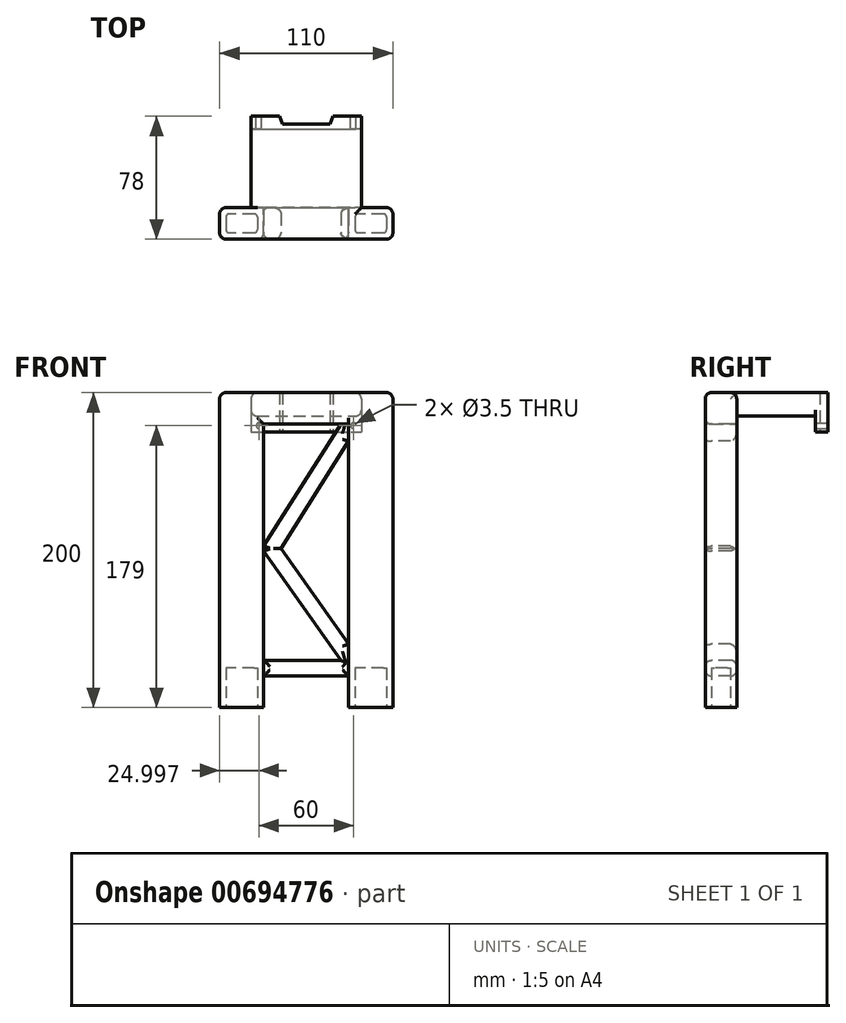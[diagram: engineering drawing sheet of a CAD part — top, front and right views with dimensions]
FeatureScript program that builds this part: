
annotation { "Feature Type Name" : "Feature", "Feature Type Description" : "" }
export const myFeature = defineFeature(function(context is Context, id is Id, definition is map)
    precondition{}
    {
        {
            var Q0;
            Q0=qCreatedBy(makeId("Top.planeOp"),FACE);
            var sketch = newSketch(context, id + "F0", { "sketchPlane" : qUnion([Q0])});
            skLineSegment(sketch, "E0.bottom", {"start": v(-48.83, 24.85) * mm, "end": v(-30.83, 24.85) * mm});
            skLineSegment(sketch, "E0.top", {"start": v(-48.83, 16.85) * mm, "end": v(21.17, 16.85) * mm});
            skLineSegment(sketch, "E0.left", {"start": v(-48.83, 24.85) * mm, "end": v(-48.83, 16.85) * mm});
            skLineSegment(sketch, "E0.right", {"start": v(21.17, 24.85) * mm, "end": v(21.17, 16.85) * mm});
            skLineSegment(sketch, "E1", {"start": v(-30.83, 24.85) * mm, "end": v(-28.83, 19.85) * mm});
            skLineSegment(sketch, "E2", {"start": v(-28.83, 19.85) * mm, "end": v(1.17, 19.85) * mm});
            skLineSegment(sketch, "E3", {"start": v(1.17, 19.85) * mm, "end": v(3.17, 24.85) * mm});
            skLineSegment(sketch, "E4.trimOffspring", {"start": v(3.17, 24.85) * mm, "end": v(21.17, 24.85) * mm});
            skSolve(sketch);
        }
        {
            var Q0;
            Q0=makeQuery(id+"F0.imprint","IMPRINT",FACE,{"disambiguationData":[TD([[makeQuery(id+"F0.imprint","IMPRINT",EDGE,{"derivedFrom":sQuery(id+"F0.wireOp",EDGE,"E0.bottom")}),-1.0]])]});
            extrude(context, id + "F1", {"entities" : qUnion([Q0]), "depth" : 25 * mm, "offsetDistance" : 25 * mm});
        }
        {
            var Q0;
            Q0=makeQuery(id+"F1.opExtrude","SWEPT_FACE",FACE,{"disambiguationData":[OSD([sQuery(id+"F0.wireOp",EDGE,"E0.bottom")])]});
            var sketch = newSketch(context, id + "F2", { "sketchPlane" : qUnion([Q0])});
            skCircle(sketch, "E5", {"center": v(-16.17, 4) * mm, "radius": 1.75 * mm});
            skCircle(sketch, "E6", {"center": v(43.83, 4) * mm, "radius": 1.75 * mm});
            skSolve(sketch);
        }
        {
            var Q0;
            Q0=makeQuery(id+"F2.imprint","IMPRINT",FACE,{"disambiguationData":[TD([[makeQuery(id+"F2.imprint","IMPRINT",EDGE,{"derivedFrom":sQuery(id+"F2.wireOp",EDGE,"E5")}),1.0]])]});
            var Q1;
            Q1=makeQuery(id+"F2.imprint","IMPRINT",FACE,{"disambiguationData":[TD([[makeQuery(id+"F2.imprint","IMPRINT",EDGE,{"derivedFrom":sQuery(id+"F2.wireOp",EDGE,"E6")}),1.0]])]});
            extrude(context, id + "F3", {"entities" : qUnion([Q0, Q1]), "operationType" : NewBodyOperationType.REMOVE, "oppositeDirection" : true, "depth" : 25 * mm, "offsetDistance" : 25 * mm});
        }
        {
            var Q0;
            Q0=makeQuery(id+"F1.opExtrude","SWEPT_FACE",FACE,{"disambiguationData":[OSD([sQuery(id+"F0.wireOp",EDGE,"E0.top")])]});
            var sketch = newSketch(context, id + "F4", { "sketchPlane" : qUnion([Q0])});
            skLineSegment(sketch, "E7.bottom", {"start": v(-48.83, 25) * mm, "end": v(21.17, 25) * mm});
            skLineSegment(sketch, "E7.top", {"start": v(-48.83, 10) * mm, "end": v(21.17, 10) * mm});
            skLineSegment(sketch, "E7.left", {"start": v(-48.83, 25) * mm, "end": v(-48.83, 10) * mm});
            skLineSegment(sketch, "E7.right", {"start": v(21.17, 25) * mm, "end": v(21.17, 10) * mm});
            skSolve(sketch);
        }
        {
            var Q0;
            Q0=makeQuery(id+"F4.imprint","IMPRINT",FACE,{"disambiguationData":[TD([[makeQuery(id+"F4.imprint","IMPRINT",EDGE,{"derivedFrom":sQuery(id+"F4.wireOp",EDGE,"E7.bottom")}),-1.0]])]});
            extrude(context, id + "F5", {"entities" : qUnion([Q0]), "operationType" : NewBodyOperationType.ADD, "depth" : 50 * mm, "offsetDistance" : 25 * mm});
        }
        {
            var Q0;
            Q0=makeQuery(id+"F5.boolean.opBoolean","MERGE",FACE,{"derivedFrom":[makeQuery(id+"F1.opExtrude","SWEPT_FACE",FACE,{"disambiguationData":[OSD([sQuery(id+"F0.wireOp",EDGE,"E0.right")])]}),makeQuery(id+"F5.opExtrude","SWEPT_FACE",FACE,{"disambiguationData":[OSD([sQuery(id+"F4.wireOp",EDGE,"E7.right")])]})]});
            var sketch = newSketch(context, id + "F6", { "sketchPlane" : qUnion([Q0])});
            skLineSegment(sketch, "E8.bottom", {"start": v(-33.15, 25) * mm, "end": v(-53.15, 25) * mm});
            skLineSegment(sketch, "E8.top", {"start": v(-33.15, -175) * mm, "end": v(-53.15, -175) * mm});
            skLineSegment(sketch, "E8.left", {"start": v(-33.15, 25) * mm, "end": v(-33.15, -175) * mm});
            skLineSegment(sketch, "E8.right", {"start": v(-53.15, 25) * mm, "end": v(-53.15, -175) * mm});
            skSolve(sketch);
        }
        {
            var Q0;
            {var subQ1=sQuery(id+"F6.wireOp",EDGE,"E8.bottom");Q0=makeQuery(id+"F6.imprint","IMPRINT",FACE,{"disambiguationData":[TD([[makeQuery(id+"F6.imprint","IMPRINT",EDGE,{"derivedFrom":subQ1}),1.0]])]});}
            extrude(context, id + "F7", {"entities" : qUnion([Q0]), "operationType" : NewBodyOperationType.ADD, "depth" : 20 * mm, "offsetDistance" : 25 * mm, "hasSecondDirection" : true, "secondDirectionOppositeDirection" : true, "secondDirectionDepth" : 90 * mm});
        }
        {
            var Q0;
            Q0=makeQuery(id+"F7.opExtrude","SWEPT_FACE",FACE,{"disambiguationData":[OSD([sQuery(id+"F6.wireOp",EDGE,"E8.left")])]});
            var sketch = newSketch(context, id + "F8", { "sketchPlane" : qUnion([Q0])});
            skLineSegment(sketch, "E9.bottom", {"start": v(-13.17, 5) * mm, "end": v(40.83, 5) * mm});
            skLineSegment(sketch, "E9.top", {"start": v(-13.17, -175) * mm, "end": v(40.83, -175) * mm});
            skLineSegment(sketch, "E9.left", {"start": v(-13.17, 5) * mm, "end": v(-13.17, -175) * mm});
            skLineSegment(sketch, "E9.right", {"start": v(40.83, 5) * mm, "end": v(40.83, -175) * mm});
            skSolve(sketch);
        }
        {
            var Q0;
            Q0=makeQuery(id+"F8.imprint","IMPRINT",FACE,{"disambiguationData":[TD([[makeQuery(id+"F8.imprint","IMPRINT",EDGE,{"derivedFrom":sQuery(id+"F8.wireOp",EDGE,"E9.bottom")}),-1.0]])]});
            extrude(context, id + "F9", {"entities" : qUnion([Q0]), "operationType" : NewBodyOperationType.REMOVE, "oppositeDirection" : true, "depth" : 25 * mm, "offsetDistance" : 25 * mm});
        }
        {
            var Q0;
            {var subQ2=sQuery(id+"F6.wireOp",EDGE,"E8.top");Q0=makeQuery(id+"F9.boolean.opBoolean","SPLIT",FACE,{"disambiguationData":[TD([makeQuery(id+"F9.opExtrude","SWEPT_FACE",FACE,{"disambiguationData":[OSD([sQuery(id+"F8.wireOp",EDGE,"E9.left")])]})])],"derivedFrom":makeQuery(id+"F7.opExtrude","SWEPT_FACE",FACE,{"disambiguationData":[OSD([subQ2])]})});}
            var sketch = newSketch(context, id + "F10", { "sketchPlane" : qUnion([Q0])});
            skLineSegment(sketch, "E10.bottom", {"start": v(35.17, 37.15) * mm, "end": v(19.17, 37.15) * mm});
            skLineSegment(sketch, "E10.top", {"start": v(35.17, 49.15) * mm, "end": v(19.17, 49.15) * mm});
            skLineSegment(sketch, "E10.left", {"start": v(37.17, 39.15) * mm, "end": v(37.17, 47.15) * mm});
            skLineSegment(sketch, "E10.right", {"start": v(17.17, 39.15) * mm, "end": v(17.17, 47.15) * mm});
            skLineSegment(sketch, "E11.bottom", {"start": v(-46.83, 37.15) * mm, "end": v(-62.83, 37.15) * mm});
            skLineSegment(sketch, "E11.top", {"start": v(-46.83, 49.15) * mm, "end": v(-62.83, 49.15) * mm});
            skLineSegment(sketch, "E11.left", {"start": v(-44.83, 39.15) * mm, "end": v(-44.83, 47.15) * mm});
            skLineSegment(sketch, "E11.right", {"start": v(-64.83, 39.15) * mm, "end": v(-64.83, 47.15) * mm});
            skPoint(sketch, "E12.visualSharp", {"position": v(-64.83, 37.15) * mm});
            skArc(sketch, "E12.filletArc", {"start": v(-64.83, 39.15) * mm, "mid": v(-64.25, 37.74) * mm, "end": v(-62.83, 37.15) * mm});
            skPoint(sketch, "E13.visualSharp", {"position": v(-64.83, 49.15) * mm});
            skArc(sketch, "E13.filletArc", {"start": v(-62.83, 49.15) * mm, "mid": v(-64.25, 48.56) * mm, "end": v(-64.83, 47.15) * mm});
            skPoint(sketch, "E14.visualSharp", {"position": v(-44.83, 49.15) * mm});
            skArc(sketch, "E14.filletArc", {"start": v(-44.83, 47.15) * mm, "mid": v(-45.42, 48.56) * mm, "end": v(-46.83, 49.15) * mm});
            skPoint(sketch, "E15.visualSharp", {"position": v(-44.83, 37.15) * mm});
            skArc(sketch, "E15.filletArc", {"start": v(-46.83, 37.15) * mm, "mid": v(-45.42, 37.74) * mm, "end": v(-44.83, 39.15) * mm});
            skPoint(sketch, "E16.visualSharp", {"position": v(17.17, 37.15) * mm});
            skArc(sketch, "E16.filletArc", {"start": v(17.17, 39.15) * mm, "mid": v(17.75, 37.74) * mm, "end": v(19.17, 37.15) * mm});
            skPoint(sketch, "E17.visualSharp", {"position": v(37.17, 37.15) * mm});
            skArc(sketch, "E17.filletArc", {"start": v(35.17, 37.15) * mm, "mid": v(36.58, 37.74) * mm, "end": v(37.17, 39.15) * mm});
            skPoint(sketch, "E18.visualSharp", {"position": v(37.17, 49.15) * mm});
            skArc(sketch, "E18.filletArc", {"start": v(37.17, 47.15) * mm, "mid": v(36.58, 48.56) * mm, "end": v(35.17, 49.15) * mm});
            skPoint(sketch, "E19.visualSharp", {"position": v(17.17, 49.15) * mm});
            skArc(sketch, "E19.filletArc", {"start": v(19.17, 49.15) * mm, "mid": v(17.75, 48.56) * mm, "end": v(17.17, 47.15) * mm});
            skSolve(sketch);
        }
        {
            var Q0;
            Q0=makeQuery(id+"F7.opExtrude","SWEPT_FACE",FACE,{"disambiguationData":[OSD([sQuery(id+"F6.wireOp",EDGE,"E8.right")])]});
            var sketch = newSketch(context, id + "F11", { "sketchPlane" : qUnion([Q0])});
            skLineSegment(sketch, "E20", {"start": v(-40.83, -155) * mm, "end": v(13.17, -155) * mm});
            skLineSegment(sketch, "E21", {"start": v(-40.83, -145) * mm, "end": v(8.17, -145) * mm});
            skLineSegment(sketch, "E22", {"start": v(8.17, -145) * mm, "end": v(-40.83, -75.6) * mm});
            skLineSegment(sketch, "E23", {"start": v(-41.83, -74.12) * mm, "end": v(8.17, 5) * mm});
            skLineSegment(sketch, "E24", {"start": v(8.17, 5) * mm, "end": v(13.17, 5) * mm});
            skLineSegment(sketch, "E25.0", {"start": v(-29.83, -73.85) * mm, "end": v(13.17, -5.8) * mm});
            skLineSegment(sketch, "E25.1", {"start": v(13.17, -134.74) * mm, "end": v(-29.83, -73.85) * mm});
            skLineSegment(sketch, "E26", {"start": v(13.17, 5) * mm, "end": v(13.17, -5.8) * mm});
            skLineSegment(sketch, "E27", {"start": v(13.17, -145) * mm, "end": v(13.17, -134.74) * mm});
            skSolve(sketch);
        }
        {
            var Q0;
            {var subQ1=sQuery(id+"F11.wireOp",EDGE,"E20");Q0=makeQuery(id+"F11.imprint","IMPRINT",FACE,{"disambiguationData":[TD([[makeQuery(id+"F11.imprint","IMPRINT",EDGE,{"derivedFrom":subQ1}),1.0]])]});}
            extrude(context, id + "F12", {"entities" : qUnion([Q0]), "oppositeDirection" : true, "depth" : 20 * mm, "offsetDistance" : 25 * mm});
        }
        {
            var Q0;
            Q0=makeQuery(id+"F10.imprint","IMPRINT",FACE,{"disambiguationData":[TD([[makeQuery(id+"F10.imprint","IMPRINT",EDGE,{"derivedFrom":sQuery(id+"F10.wireOp",EDGE,"E11.bottom")}),-1.0]])]});
            var Q1;
            Q1=makeQuery(id+"F10.imprint","IMPRINT",FACE,{"disambiguationData":[TD([[makeQuery(id+"F10.imprint","IMPRINT",EDGE,{"derivedFrom":sQuery(id+"F10.wireOp",EDGE,"E10.bottom")}),-1.0]])]});
            extrude(context, id + "F13", {"entities" : qUnion([Q0, Q1]), "operationType" : NewBodyOperationType.REMOVE, "oppositeDirection" : true, "depth" : 25 * mm, "offsetDistance" : 25 * mm});
        }
        {
            var Q0;
            Q0=makeQuery(id+"F9.boolean.opBoolean","COPY",EDGE,{"derivedFrom":makeQuery(id+"F9.opExtrude","CAP_EDGE",EDGE,{"disambiguationData":[OSD([sQuery(id+"F8.wireOp",EDGE,"E9.left")])],"isStart":true})});
            var Q1;
            Q1=makeQuery(id+"F9.boolean.opBoolean","COPY",EDGE,{"derivedFrom":makeQuery(id+"F9.opExtrude","CAP_EDGE",EDGE,{"disambiguationData":[OSD([sQuery(id+"F8.wireOp",EDGE,"E9.right")])],"isStart":true})});
            var Q2;
            Q2=makeQuery(id+"F9.boolean.opBoolean","INTERSECT",EDGE,{"derivedFrom":[makeQuery(id+"F7.opExtrude","SWEPT_FACE",FACE,{"disambiguationData":[OSD([sQuery(id+"F6.wireOp",EDGE,"E8.right")])]}),makeQuery(id+"F9.opExtrude","SWEPT_FACE",FACE,{"disambiguationData":[OSD([sQuery(id+"F8.wireOp",EDGE,"E9.right")])]})]});
            var Q3;
            Q3=makeQuery(id+"F7.opExtrude","CAP_EDGE",EDGE,{"disambiguationData":[OSD([sQuery(id+"F6.wireOp",EDGE,"E8.left")])],"isStart":true});
            var Q4;
            Q4=makeQuery(id+"F7.opExtrude","CAP_EDGE",EDGE,{"disambiguationData":[OSD([sQuery(id+"F6.wireOp",EDGE,"E8.left")])],"isStart":false});
            var Q5;
            Q5=makeQuery(id+"F7.opExtrude","CAP_EDGE",EDGE,{"disambiguationData":[OSD([sQuery(id+"F6.wireOp",EDGE,"E8.right")])],"isStart":false});
            var Q6;
            Q6=makeQuery(id+"F12.opExtrude","CAP_EDGE",EDGE,{"disambiguationData":[OSD([sQuery(id+"F11.wireOp",EDGE,"E23")])],"isStart":false});
            var Q7;
            Q7=makeQuery(id+"F12.opExtrude","CAP_EDGE",EDGE,{"disambiguationData":[OSD([sQuery(id+"F11.wireOp",EDGE,"E25.0")])],"isStart":false});
            var Q8;
            Q8=makeQuery(id+"F12.opExtrude","CAP_EDGE",EDGE,{"disambiguationData":[OSD([sQuery(id+"F11.wireOp",EDGE,"E25.0")])],"isStart":true});
            var Q9;
            Q9=makeQuery(id+"F12.opExtrude","CAP_EDGE",EDGE,{"disambiguationData":[OSD([sQuery(id+"F11.wireOp",EDGE,"E25.1")])],"isStart":false});
            var Q10;
            Q10=makeQuery(id+"F12.opExtrude","CAP_EDGE",EDGE,{"disambiguationData":[OSD([sQuery(id+"F11.wireOp",EDGE,"E25.1")])],"isStart":true});
            var Q11;
            Q11=makeQuery(id+"F12.opExtrude","CAP_EDGE",EDGE,{"disambiguationData":[OSD([sQuery(id+"F11.wireOp",EDGE,"E22")])],"isStart":false});
            var Q12;
            Q12=makeQuery(id+"F12.opExtrude","CAP_EDGE",EDGE,{"disambiguationData":[OSD([sQuery(id+"F11.wireOp",EDGE,"E22")])],"isStart":true});
            var Q13;
            Q13=makeQuery(id+"F12.opExtrude","CAP_FACE",FACE,{"disambiguationData":[OSD([sQuery(id+"F6.wireOp",EDGE,"E8.right"),sQuery(id+"F8.wireOp",EDGE,"E9.left"),sQuery(id+"F8.wireOp",EDGE,"E9.right"),sQuery(id+"F11.wireOp",EDGE,"E20"),sQuery(id+"F11.wireOp",EDGE,"E21"),sQuery(id+"F11.wireOp",EDGE,"E22"),sQuery(id+"F11.wireOp",EDGE,"E23"),sQuery(id+"F11.wireOp",EDGE,"E24"),sQuery(id+"F11.wireOp",EDGE,"E25.0"),sQuery(id+"F11.wireOp",EDGE,"E25.1"),sQuery(id+"F11.wireOp",EDGE,"E26"),sQuery(id+"F11.wireOp",EDGE,"E27")])],"isStart":true});
            var Q14;
            Q14=makeQuery(id+"F12.opExtrude","CAP_EDGE",EDGE,{"disambiguationData":[OSD([sQuery(id+"F11.wireOp",EDGE,"E21")])],"isStart":false});
            var Q15;
            Q15=makeQuery(id+"F12.opExtrude","CAP_EDGE",EDGE,{"disambiguationData":[OSD([sQuery(id+"F11.wireOp",EDGE,"E20")])],"isStart":false});
            var Q16;
            Q16=makeQuery(id+"F7.opExtrude","CAP_EDGE",EDGE,{"disambiguationData":[OSD([sQuery(id+"F6.wireOp",EDGE,"E8.right")])],"isStart":true});
            var Q17;
            Q17=makeQuery(id+"F7.opExtrude","SWEPT_EDGE",EDGE,{"disambiguationData":[OSD([sQuery(id+"F6.wireOp",EDGE,"E8.bottom"),sQuery(id+"F6.wireOp",EDGE,"E8.right")])]});
            var Q18;
            Q18=makeQuery(id+"F7.opExtrude","CAP_EDGE",EDGE,{"disambiguationData":[OSD([sQuery(id+"F6.wireOp",EDGE,"E8.bottom")])],"isStart":false});
            var Q19;
            {var subQ0=sQuery(id+"F0.wireOp",EDGE,"E0.right");var subQ1=sQuery(id+"F4.wireOp",EDGE,"E7.right");var subQ2=sQuery(id+"F6.wireOp",EDGE,"E8.bottom");var subQ3=sQuery(id+"F4.wireOp",EDGE,"E7.bottom");var subQ4=sQuery(id+"F6.wireOp",EDGE,"E8.left");Q19=makeQuery(id+"F7.boolean.opBoolean","SPLIT",EDGE,{"disambiguationData":[TD([makeQuery(id+"F1.opExtrude","SWEPT_FACE",FACE,{"disambiguationData":[OSD([subQ0])]})])],"derivedFrom":makeQuery(id+"F7.opExtrude","SWEPT_EDGE",EDGE,{"disambiguationData":[OSD([subQ0,subQ3,subQ1,subQ2,subQ4])]})});}
            var Q20;
            Q20=makeQuery(id+"F5.boolean.opBoolean","MERGE",EDGE,{"derivedFrom":[makeQuery(id+"F1.opExtrude","CAP_EDGE",EDGE,{"disambiguationData":[OSD([sQuery(id+"F0.wireOp",EDGE,"E0.right")])],"isStart":false}),makeQuery(id+"F5.opExtrude","SWEPT_EDGE",EDGE,{"disambiguationData":[OSD([sQuery(id+"F4.wireOp",EDGE,"E7.bottom"),sQuery(id+"F4.wireOp",EDGE,"E7.right")])]})]});
            var Q21;
            Q21=makeQuery(id+"F5.boolean.opBoolean","MERGE",EDGE,{"derivedFrom":[makeQuery(id+"F1.opExtrude","CAP_EDGE",EDGE,{"disambiguationData":[OSD([sQuery(id+"F0.wireOp",EDGE,"E0.left")])],"isStart":false}),makeQuery(id+"F5.opExtrude","SWEPT_EDGE",EDGE,{"disambiguationData":[OSD([sQuery(id+"F4.wireOp",EDGE,"E7.bottom"),sQuery(id+"F4.wireOp",EDGE,"E7.left")])]})]});
            var Q22;
            Q22=makeQuery(id+"F5.opExtrude","SWEPT_EDGE",EDGE,{"disambiguationData":[OSD([sQuery(id+"F0.wireOp",EDGE,"E0.top"),sQuery(id+"F0.wireOp",EDGE,"E0.right"),sQuery(id+"F4.wireOp",EDGE,"E7.top"),sQuery(id+"F4.wireOp",EDGE,"E7.right")])]});
            var Q23;
            Q23=makeQuery(id+"F5.opExtrude","SWEPT_EDGE",EDGE,{"disambiguationData":[OSD([sQuery(id+"F0.wireOp",EDGE,"E0.top"),sQuery(id+"F0.wireOp",EDGE,"E0.left"),sQuery(id+"F4.wireOp",EDGE,"E7.top"),sQuery(id+"F4.wireOp",EDGE,"E7.left")])]});
            var Q24;
            Q24=makeQuery(id+"F9.boolean.opBoolean","INTERSECT",EDGE,{"derivedFrom":[makeQuery(id+"F7.opExtrude","SWEPT_FACE",FACE,{"disambiguationData":[OSD([sQuery(id+"F6.wireOp",EDGE,"E8.right")])]}),makeQuery(id+"F9.opExtrude","SWEPT_FACE",FACE,{"disambiguationData":[OSD([sQuery(id+"F8.wireOp",EDGE,"E9.bottom")])]})]});
            var Q25;
            Q25=makeQuery(id+"F9.boolean.opBoolean","COPY",EDGE,{"derivedFrom":makeQuery(id+"F9.opExtrude","CAP_EDGE",EDGE,{"disambiguationData":[OSD([sQuery(id+"F8.wireOp",EDGE,"E9.bottom")])],"isStart":true})});
            var Q26;
            Q26=makeQuery(id+"F7.opExtrude","CAP_EDGE",EDGE,{"disambiguationData":[OSD([sQuery(id+"F6.wireOp",EDGE,"E8.bottom")])],"isStart":true});
            fillet(context, id + "F14", {"entities" : qUnion([Q0, Q1, Q2, Q3, Q4, Q5, Q6, Q7, Q8, Q9, Q10, Q11, Q12, Q13, Q14, Q15, Q16, Q17, Q18, Q19, Q20, Q21, Q22, Q23, Q24, Q25, Q26]), "radius" : 4 * mm, "tangentPropagation" : true, "allowEdgeOverflow" : false});
        }
    });
